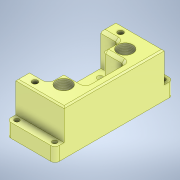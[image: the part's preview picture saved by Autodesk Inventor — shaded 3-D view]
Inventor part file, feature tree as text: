
AUTODESK INVENTOR PART (.ipt)
format: ipt  version: 2021 (Build 250183000, 183)  size: 839,168 bytes
history: native  units: mm
features: sketch x12, projected_geometry x11, extrude x10, chamfer x9, hole x6, fillet x4, plane x1
ambient origin geometry x8: Origin, YZ Plane, XZ Plane, XY Plane, X Axis, Y Axis, Z Axis, Center Point
bodies: Solid1 (feature_tree)
feature tree (53):
  extrude  "Extrusion1"  Depth=71.5mm
  hole  "Hole1"  [1 undecoded]
  hole  "Hole2"  [1 undecoded]
  extrude  "Extrusion2"  Depth=3.0mm
  hole  "Hole3"  [1 undecoded]
  extrude  "Extrusion3"  Depth=2.0mm
  extrude  "Extrusion5"  Depth=5.7mm
  chamfer  "Chamfer1"  Distance=24.5mm
  chamfer  "Chamfer2"  Distance=2.0mm
  extrude  "Extrusion6"  Depth=11.5mm
  extrude  "Extrusion7"  Depth=1.0mm
  fillet  "Fillet11"  Radius=4.0mm
  hole  "Hole4"  [1 undecoded]
  hole  "Hole5"  [1 undecoded]
  extrude  "Extrusion8"  Depth=16.0mm
  hole  "Hole6"  [1 undecoded]
  extrude  "Extrusion9"  Depth=50.0mm
  plane  "Work Plane2"
  chamfer  "Chamfer3"  Distance=12.5mm
  chamfer  "Chamfer4"  Distance=2.0mm
  chamfer  "Chamfer5"  Distance=2.0mm
  extrude  "Extrusion11"  Depth=9.0mm
  extrude  "Extrusion13"  Depth=23.0mm
  fillet  "Fillet10"  Radius=5.5mm
  fillet  "Fillet12"  Radius=19.0mm
  fillet  "Fillet13"  Radius=77.5mm
  chamfer  "Chamfer7"  Distance=27.0mm
  chamfer  "Chamfer8"  Distance=10.0mm
  chamfer  "Chamfer9"  Distance=9.9mm
  chamfer  "Chamfer10"  Distance=1.9mm
  sketch  "Sketch1"  dims[d0=34.5mm d1=71.5mm]
  sketch  "Sketch4"  dims[d2=22.0mm d3=0.0mm d5=44.0mm]
  projected_geometry  "Projected Loop1"
  projected_geometry  "Projected Loop2"
  sketch  "Sketch5"  dims[d7=10.2mm d8=6.0mm d9=4.0mm d10=2.0mm d11=90.0deg d12=8.0mm d13=20.594885mm]
  sketch  "Sketch7"  dims[d14=10.917mm d15=15.0mm d16=4.0mm d17=2.0mm d18=90.0deg d19=15.0mm d20=20.594885mm d21=84.5mm]
  projected_geometry  "Projected Loop4"
  projected_geometry  "Projected Loop5"
  sketch  "Sketch9"  dims[d22=34.5mm d23=3.0mm]
  projected_geometry  "Projected Loop6"
  sketch  "Sketch11"  dims[d24=9.85mm d25=0.0mm]
  sketch  "Sketch12"  dims[d26=4.4mm d27=15.0mm d28=4.0mm d29=2.0mm d30=90.0deg d31=15.0mm d32=20.594885mm d33=28.0mm]
  sketch  "Sketch13"  dims[d34=28.0mm d35=2.0mm]
  projected_geometry  "Projected Loop7"
  projected_geometry  "Projected Loop8"
  projected_geometry  "Projected Loop9"
  projected_geometry  "Projected Loop10"
  sketch  "Sketch14"  dims[d38=23.7mm d39=0.0mm d49=5.7mm]
  projected_geometry  "Projected Loop11"
  sketch  "Sketch15"  dims[d50=18.3mm d51=24.5mm d52=0.0mm d53=2.0mm d54=2.0mm d55=4.886922mm]
  projected_geometry  "Projected Loop13"
  sketch  "Sketch17"  dims[d56=2.0mm d57=2.0mm d58=4.886922mm d59=11.5mm]
  sketch  "Sketch19"  dims[d60=11.5mm d62=1.0mm d64=4.0mm d65=-3.490659mm d67=1.5mm d68=13.0mm d70=16.0mm d71=50.0mm d79=4.0mm d80=-3.490659mm d81=50.0mm d82=12.5mm d83=2.0mm d84=2.0mm d86=9.0mm d87=23.0mm d88=5.5mm d89=19.0mm d90=4.0mm d91=6.0mm d92=4.0mm d93=2.0mm d94=90.0deg d95=5.0mm d96=0.0mm d97=77.5mm d98=27.0mm d99=3.4mm d100=6.0mm d101=6.0mm d102=2.7mm d103=90.0deg d104=5.0mm d105=0.0mm d106=10.0mm d107=0.0mm d112=4.0mm d113=6.0mm d114=4.0mm d115=2.0mm d116=90.0deg d117=5.0mm d118=0.0mm d121=9.9mm d122=1.9mm d123=4.0mm d124=-3.490659mm d125=22.0mm d126=3.2mm d128=-7.0mm d137=10.2mm d138=2.85mm d140=0.5mm d141=2.0mm d142=45.0deg d143=5.15mm d144=5.15mm d145=11.95mm d146=2.0mm d147=2.0mm d148=45.0deg d149=1.0mm d150=2.0mm d151=45.0deg d155=1.85mm d156=2.0mm d157=1.85mm d158=2.0mm d159=1.0mm d160=1.0mm d161=5.5mm d162=19.0mm d163=19.0mm d164=15.0mm d165=13.0mm d166=11.05mm d167=6.8mm d168=6.8mm d169=6.8mm d170=6.2mm d171=11.75mm d172=8.2mm d173=1.0mm d174=16.0mm d175=10.0mm d176=0.0mm d179=4.2mm d180=3.490659mm d181=2.0mm d182=1.5mm d183=1.5mm d184=1.5mm d185=2.0mm d186=2.0mm d187=2.0mm d188=0.5mm d189=2.0mm d190=45.0deg d191=11.5mm d192=0.5mm d193=2.0mm d194=45.0deg d195=0.5mm d196=2.0mm d197=45.0deg d198=0.5mm d199=2.0mm d200=45.0deg]
note: 6 required parameter values undecoded (feature->parameter linkage not recoverable at this tier; creation-order binding heuristic only, values carry confidence <= 0.55)
